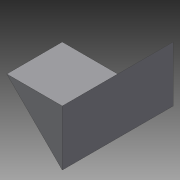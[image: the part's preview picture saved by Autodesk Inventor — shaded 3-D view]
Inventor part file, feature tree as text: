
AUTODESK INVENTOR PART (.ipt)
format: ipt  version: 2015 (Build 190159000, 159)  size: 78,336 bytes
history: native  units: in
note: dims shown in document units (in); Inventor stores cm internally (conversion verified against a paired STEP export)
features: extrude x2, sketch x2
ambient origin geometry x8: Origin, YZ Plane, XZ Plane, XY Plane, X Axis, Y Axis, Z Axis, Center Point
bodies: Solid1 (feature_tree)
feature tree (4):
  extrude  "Extrusion1"  TaperAngle=45.0deg  [1 undecoded]
  extrude  "Extrusion2"  Depth=1.0in TaperAngle=0.0deg
  sketch  "Sketch1"  dims[d0=45.0deg d1=45.0deg]
  sketch  "Sketch2"  dims[d2=1.0in d3=1.0in d4=0.0in d5=1.0in d6=1.0in d7=0.0in]
note: 1 required parameter value undecoded (feature->parameter linkage not recoverable at this tier; creation-order binding heuristic only, values carry confidence <= 0.55)
